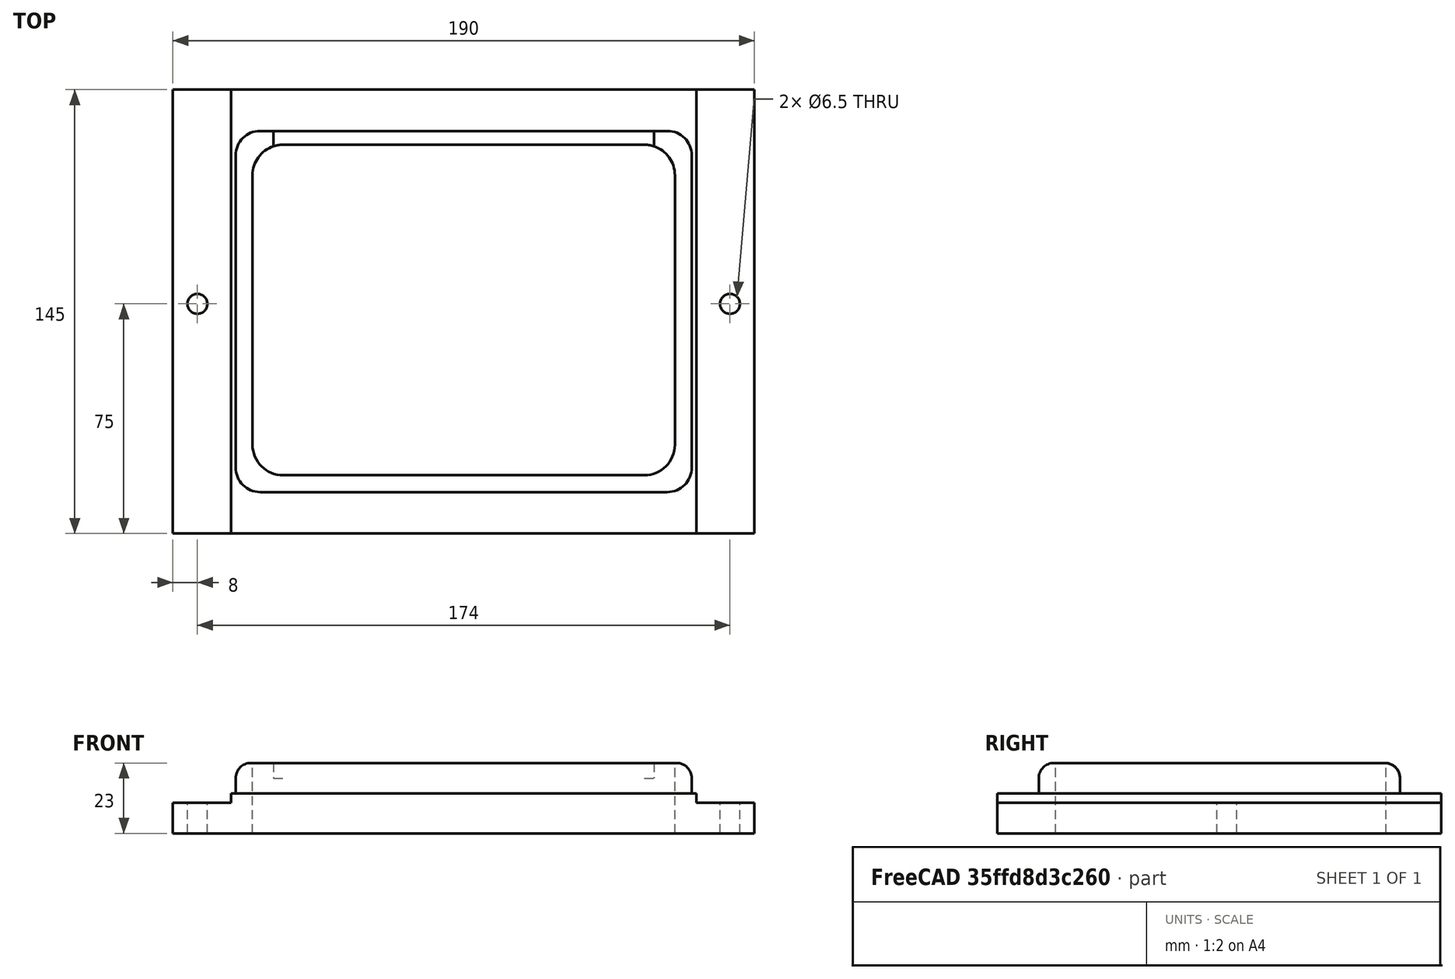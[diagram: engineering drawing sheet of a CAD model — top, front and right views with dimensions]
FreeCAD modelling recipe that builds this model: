
FCSTD DOCUMENT  (FreeCAD 0.15R4671 (Git))
Label: cubeta superior
License: All rights reserved
LicenseURL: http://es.wikipedia.org/wiki/Todos_los_derechos_reservados
objects: Part::Box×4, Part::Fillet×3, Part::Cut×2, Part::MultiFuse×1, Part::Cylinder×1, Part::FeaturePython×1
note: 12 computed .brp shape members not serialized (recipe doc carries the construction recipe); baked Part::Feature solids carry a one-line shape summary decoded from their .brp

FEATURE [Part::Box] Box  label="Cubo"
  Height = 10
  Length = 190
  Width = 145
FEATURE [Part::Box] Box001  label="Cubo001"
  Height = 10
  Length = 152
  Placement = pos=(19,0,3) rot=(0,0,1;0rad)
  Width = 145
FEATURE [Part::Box] Box002  label="Cubo002"
  Height = 20
  Length = 149
  Placement = pos=(20.5,13.5,3) rot=(0,0,1;0rad)
  Width = 118
FEATURE [Part::Box] Box003  label="Cubo003"
  Height = 37
  Length = 138
  Placement = pos=(26,19,-4) rot=(0,0,1;0rad)
  Width = 108
FEATURE [Part::MultiFuse] Fusion
  Shapes = -> [Box002,Box001,Box]
FEATURE [Part::Cut] Cut
  Base = -> Fusion
  Tool = -> Box003
FEATURE [Part::Fillet] Fillet
  Base = -> Cut
  Edges = 4 edges r=10: [Edge33,Edge35,Edge37,Edge39]
FEATURE [Part::Fillet] Fillet001
  Base = -> Fillet
  Edges = 4 edges r=8: [Edge57,Edge58,Edge59,Edge60]
FEATURE [Part::Fillet] Fillet002
  Base = -> Fillet001
  Edges = 8 edges r=5: [Edge1,Edge2,Edge3,Edge4,Edge5,Edge6,Edge7,Edge8]
FEATURE [Part::Cylinder] Cylinder  label="Cilindro"
  Angle = 360
  Height = 10
  Placement = pos=(8,75,0) rot=(0,0,1;0rad)
  Radius = 3.25
FEATURE [Part::FeaturePython] Array  # Draft array (typed FeaturePython)
  Angle = 360
  ArrayType = 0
  Axis = (0,0,1)
  Base = -> Cylinder
  Center = (0,0,0)
  Fuse = false
  IntervalAxis = (0,0,0)
  IntervalX = (174,0,0)
  IntervalY = (0,1,0)
  IntervalZ = (0,0,0)
  NumberPolar = 2
  NumberX = 2
  NumberY = 1
  NumberZ = 1
FEATURE [Part::Cut] Cut001
  Base = -> Fillet002
  Tool = -> Array
